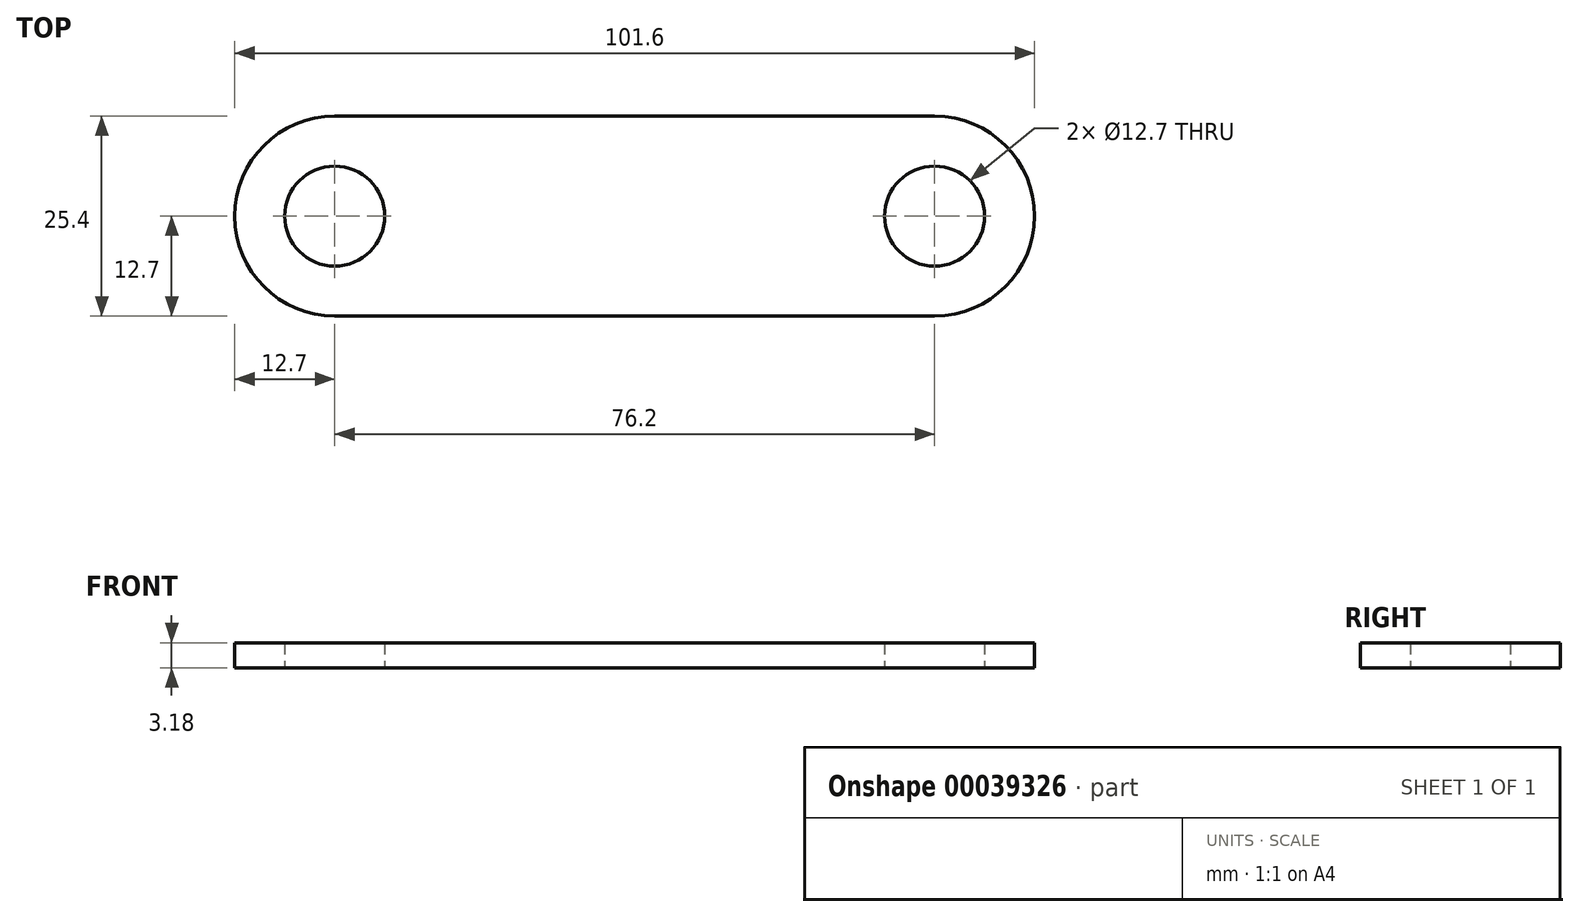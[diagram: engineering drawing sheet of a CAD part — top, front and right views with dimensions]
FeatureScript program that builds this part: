
annotation { "Feature Type Name" : "Feature", "Feature Type Description" : "" }
export const myFeature = defineFeature(function(context is Context, id is Id, definition is map)
    precondition{}
    {
        {
            var Q0;
            Q0=qCreatedBy(makeId("Top.planeOp"),FACE);
            var sketch = newSketch(context, id + "F0", { "sketchPlane" : qUnion([Q0])});
            skLineSegment(sketch, "E0.rect.bottom", {"start": v(50.8, 12.7) * mm, "end": v(-50.8, 12.7) * mm});
            skLineSegment(sketch, "E0.rect.top", {"start": v(50.8, -12.7) * mm, "end": v(-50.8, -12.7) * mm});
            skLineSegment(sketch, "E0.rect.left", {"start": v(50.8, 12.7) * mm, "end": v(50.8, -12.7) * mm});
            skLineSegment(sketch, "E0.rect.right", {"start": v(-50.8, 12.7) * mm, "end": v(-50.8, -12.7) * mm});
            skPoint(sketch, "E0.rect.middle", {"position": v(0, 0) * mm});
            skCircle(sketch, "E1", {"center": v(38.1, 0) * mm, "radius": 6.35 * mm});
            skLineSegment(sketch, "E2", {"start": v(0, 12.7) * mm, "end": v(0, -12.7) * mm, "construction": true});
            skCircle(sketch, "E3.MirrorC", {"center": v(-38.1, 0) * mm, "radius": 6.35 * mm});
            skSolve(sketch);
        }
        {
            var Q0;
            Q0=makeQuery(id+"F0.imprint","IMPRINT",FACE,{"disambiguationData":[TD([[makeQuery(id+"F0.imprint","IMPRINT",EDGE,{"derivedFrom":sQuery(id+"F0.wireOp",EDGE,"E0.rect.bottom")}),1.0]])]});
            extrude(context, id + "F1", {"entities" : qUnion([Q0]), "depth" : 3.17 * mm});
        }
        {
            var Q0;
            Q0=makeQuery(id+"F1.opExtrude","SWEPT_EDGE",EDGE,{"disambiguationData":[OSD([sQuery(id+"F0.wireOp",EDGE,"E0.rect.top"),sQuery(id+"F0.wireOp",EDGE,"E0.rect.right")])]});
            var Q1;
            Q1=makeQuery(id+"F1.opExtrude","SWEPT_EDGE",EDGE,{"disambiguationData":[OSD([sQuery(id+"F0.wireOp",EDGE,"E0.rect.top"),sQuery(id+"F0.wireOp",EDGE,"E0.rect.left")])]});
            var Q2;
            Q2=makeQuery(id+"F1.opExtrude","SWEPT_EDGE",EDGE,{"disambiguationData":[OSD([sQuery(id+"F0.wireOp",EDGE,"E0.rect.bottom"),sQuery(id+"F0.wireOp",EDGE,"E0.rect.right")])]});
            var Q3;
            Q3=makeQuery(id+"F1.opExtrude","SWEPT_EDGE",EDGE,{"disambiguationData":[OSD([sQuery(id+"F0.wireOp",EDGE,"E0.rect.bottom"),sQuery(id+"F0.wireOp",EDGE,"E0.rect.left")])]});
            fillet(context, id + "F2", {"entities" : qUnion([Q0, Q1, Q2, Q3]), "radius" : 12.7 * mm, "tangentPropagation" : true, "allowEdgeOverflow" : false});
        }
    });
